# Revit family: FU_Chair_Sandler_Varya XL 0670
name_source: partatom
category: Furniture
units: mm (PartAtom-declared; Revit-internal decimal feet)

## family parameters
Always vertical = Yes
Cut with Voids When Loaded = No
OmniClass Number = 23.40.20.00
OmniClass Title = General Furniture and Specialties
Render Appearance Source = Family Geometry
Room Calculation Point = No
Shared = No
Work Plane-Based = No

## types (1)
- Varya XL 0670
    Default Elevation = 0 mm  [stored 0 ft]
    Depth = 630 mm
    Description = Swivel chair with upholstered seat shell and 5 spoke swivel base made of cast aluminum alloy with gas lift column. The base is fitted with 65mm twin wheel swivel casters with soft tread. The seat height is adjustable.
Greenguard Gold-certified to protect indoor air quality.
    Height = 895 mm  [stored 2.93635 ft]
    Manufacturer = Sandler
    Model = Varya XL 0670
    URL = https://www.sandlerseating.com
    Width = 640 mm  [stored 2.09974 ft]

note: [stored X ft] marks values corroborated as IEEE doubles in the binary element streams (Revit-internal decimal feet)

## geometry (parser evidence)
native form markers: Sweep x12
no freeform markers — native parametric forms only
